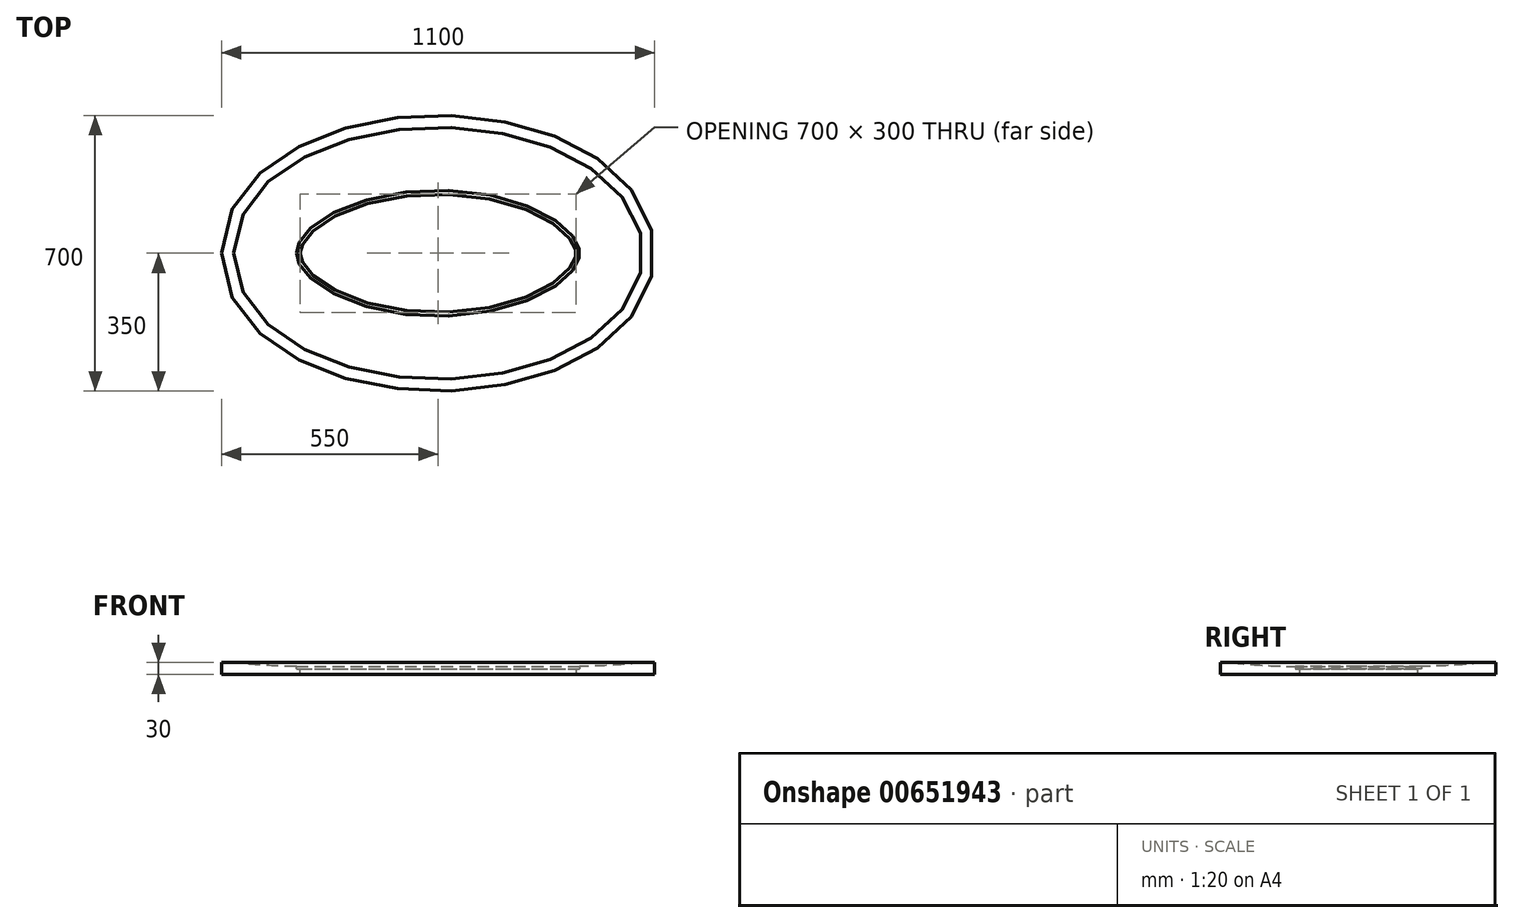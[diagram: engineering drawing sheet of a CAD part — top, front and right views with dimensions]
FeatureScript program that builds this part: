
annotation { "Feature Type Name" : "Feature", "Feature Type Description" : "" }
export const myFeature = defineFeature(function(context is Context, id is Id, definition is map)
    precondition{}
    {
        {
            var Q0;
            Q0=qCreatedBy(makeId("Top.planeOp"),FACE);
            var sketch = newSketch(context, id + "F0", { "sketchPlane" : qUnion([Q0])});
            skLineSegment(sketch, "E0", {"start": v(0, 0) * mm, "end": v(900, 0) * mm, "construction": true});
            skPoint(sketch, "E1", {"position": v(450, 0) * mm});
            skEllipse(sketch, "E2", {"center": v(450, 0) * mm, "majorRadius": 450 * mm, "minorRadius": 250 * mm, "majorAxis": v(-1, 0)});
            skSolve(sketch);
        }
        {
            var Q0;
            Q0=qCreatedBy(makeId("Front.planeOp"),FACE);
            var sketch = newSketch(context, id + "F1", { "sketchPlane" : qUnion([Q0])});
            skLineSegment(sketch, "E3.top", {"start": v(-100, -15) * mm, "end": v(100, -15) * mm});
            skLineSegment(sketch, "E3.left", {"start": v(-100, 15) * mm, "end": v(-100, -15) * mm});
            skLineSegment(sketch, "E3.right", {"start": v(100, -1) * mm, "end": v(100, -15) * mm});
            skLineSegment(sketch, "E4", {"start": v(100, -1) * mm, "end": v(90, -1) * mm});
            skLineSegment(sketch, "E5", {"start": v(90, -1) * mm, "end": v(90, 5) * mm});
            skLineSegment(sketch, "E6", {"start": v(-100, 15) * mm, "end": v(-70, 15) * mm});
            skArc(sketch, "E7", {"start": v(-70, 15) * mm, "mid": v(9.88, 8) * mm, "end": v(90, 5) * mm});
            skSolve(sketch);
        }
        {
            var Q0;
            Q0 = qSketchRegion(id + "F1", true);
            var Q1;
            Q1=sQuery(id+"F0.wireOp",EDGE,"E2");
            sweep(context, id + "F2", {"profiles" : qUnion([Q0]), "path" : qUnion([Q1])});
        }
    });
